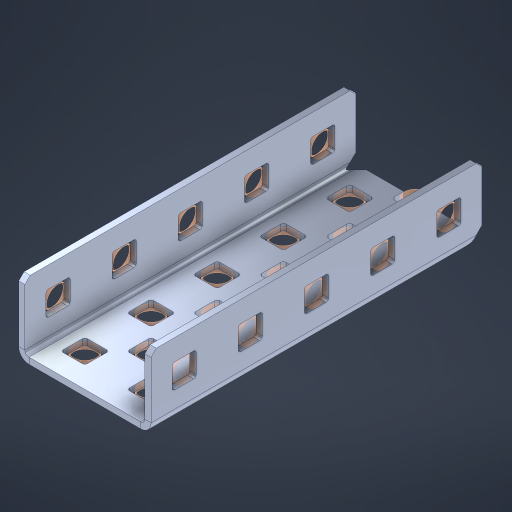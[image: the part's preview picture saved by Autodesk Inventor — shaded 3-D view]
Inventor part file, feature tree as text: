
AUTODESK INVENTOR PART (.ipt)
format: ipt  version: 2023 (Build 270158000, 158)  size: 665,088 bytes
history: native  units: in
note: dims shown in document units (in); Inventor stores cm internally (conversion verified against a paired STEP export)
features: other x32, extrude x23, sheet_metal_op x11, sketch x10, pattern_linear x2, mirror x1, chamfer x1
ambient origin geometry x8: Origin, YZ Plane, XZ Plane, XY Plane, X Axis, Y Axis, Z Axis, Center Point
bodies: Solid1 (feature_tree), Body (feature_tree)
feature tree (80):
  sheet_metal_op  "Flanges"
  other  "Flange Pattern Plane"
  other  "Flange Pattern Sketch"
  sheet_metal_op  "Flange Pattern"
  sheet_metal_op  "Body Pattern"
  pattern_linear  "Center Pattern"  Spacing1=0.0469in  [1 undecoded]
  other  "Arc Length"
  mirror  "Notch Mirror"
  pattern_linear  "Notch Pattern"  Spacing1=0.182in  [1 undecoded]
  chamfer  "End Chamfer"
  extrude  "Half Cut"  Depth=0.02in
  sketch  "Sketch1"  dims[d0=1.0in]
  other  "Plate1"
  sketch  "Sketch2"  dims[d1=2.5in]
  other  "Plate2"
  sheet_metal_op  "Bend1"
  sheet_metal_op  "Corner1"
  sketch  "Sketch3"  dims[d2=0.0469in]
  sketch  "Sketch7"  dims[d3=0.0469in]
  other  "Srf1"
  other  "Srf2"
  sketch  "Sketch8"  dims[d4=0.0234in]
  sketch  "Sketch9"  dims[d5=0.0938in]
  other  "Srf91"
  sheet_metal_op  "Body Pattern Sketch"
  other  "Srf92"
  sketch  "Sketch13"  dims[d6=0.0469in]
  sketch  "Sketch14"  dims[d7=0.5in d8=90.0deg d9=0.0312in]
  sketch  "Sketch15"  dims[d10=0.1875in]
  sketch  "Sketch16"  dims[d11=0.0469in d12=0.0469in d16=0.182in d17=0.02in d18=0.0469in d19=0.0in d20=0.25in d21=0.25in d38=1.9685in d40=0.5in d41=0.7874in d43=1.0in d46=0.172in d47=1.0in d48=0.0in d49=0.182in d50=0.02in d51=0.25in d52=0.25in d53=0.0469in d54=0.0in d55=0.172in d56=1.0in d57=0.0in d58=0.25in d60=1.9685in d62=0.5in d63=0.7874in d65=0.5in d85=0.1227in d86=0.1659in d88=0.04in d89=0.0469in d90=0.0in d91=0.04in d92=0.0491in d95=2.5in d96=0.04in d97=0.25in d98=45.0deg d99=0.25in d100=0.5in d101=0.0in d102=2.497in d106=0.182in d107=0.02in d108=0.5in d109=0.5in d110=0.0469in d111=0.0in d112=0.172in d113=0.5in d114=0.0in d117=0.5in d118=0.5in d119=0.5in]
  other  "Srf786"
  other  "Srf823"
  other  "Srf824"
  other  "Srf825"
  other  "Srf826"
  other  "Srf827"
  other  "Srf828"
  other  "Srf829"
  other  "Srf856"
  other  "Srf857"
  other  "Srf858"
  other  "Srf859"
  other  "Srf860"
  other  "Srf861"
  other  "Srf862"
  other  "Srf889"
  other  "Srf890"
  other  "Srf891"
  other  "Srf892"
  other  "Srf922"
  other  "Srf959"
  sheet_metal_op  "Flange Stamp"
  sheet_metal_op  "Flange Circle"
  sheet_metal_op  "Body Stamp"
  sheet_metal_op  "Body Circle"
  other  "Center Stamp"
  other  "Center Circle"
  sheet_metal_op  "Notch"
  extrude  "ExtrusionSrf2"  Depth=0.0469in
  extrude  "ExtrusionSrf92"  TaperAngle=0.0deg  [1 undecoded]
  extrude  "ExtrusionSrf823"  Depth=0.5in
  extrude  "ExtrusionSrf824"  Depth=0.5in
  extrude  "ExtrusionSrf825"  Depth=0.5in
  extrude  "ExtrusionSrf826"  Depth=0.5in
  extrude  "ExtrusionSrf827"  Depth=1.0in TaperAngle=0.0deg
  extrude  "ExtrusionSrf828"  Depth=0.5in
  extrude  "ExtrusionSrf829"  Depth=0.02in
  extrude  "ExtrusionSrf856"  Depth=0.5in
  extrude  "ExtrusionSrf857"  Depth=0.5in
  extrude  "ExtrusionSrf858"  Depth=0.0469in
  extrude  "ExtrusionSrf859"  TaperAngle=0.0deg  [1 undecoded]
  extrude  "ExtrusionSrf860"  Depth=0.5in
  extrude  "ExtrusionSrf861"  Depth=1.0in TaperAngle=0.0deg
  extrude  "ExtrusionSrf862"  Depth=0.5in
  extrude  "ExtrusionSrf889"  Depth=0.5in
  extrude  "ExtrusionSrf890"  Depth=0.5in
  extrude  "ExtrusionSrf891"  Depth=0.5in
  extrude  "ExtrusionSrf892"  Depth=0.5in
  extrude  "ExtrusionSrf922"  Depth=0.5in
  extrude  "ExtrusionSrf959"  Depth=0.0469in
note: 4 required parameter values undecoded (feature->parameter linkage not recoverable at this tier; creation-order binding heuristic only, values carry confidence <= 0.55)
